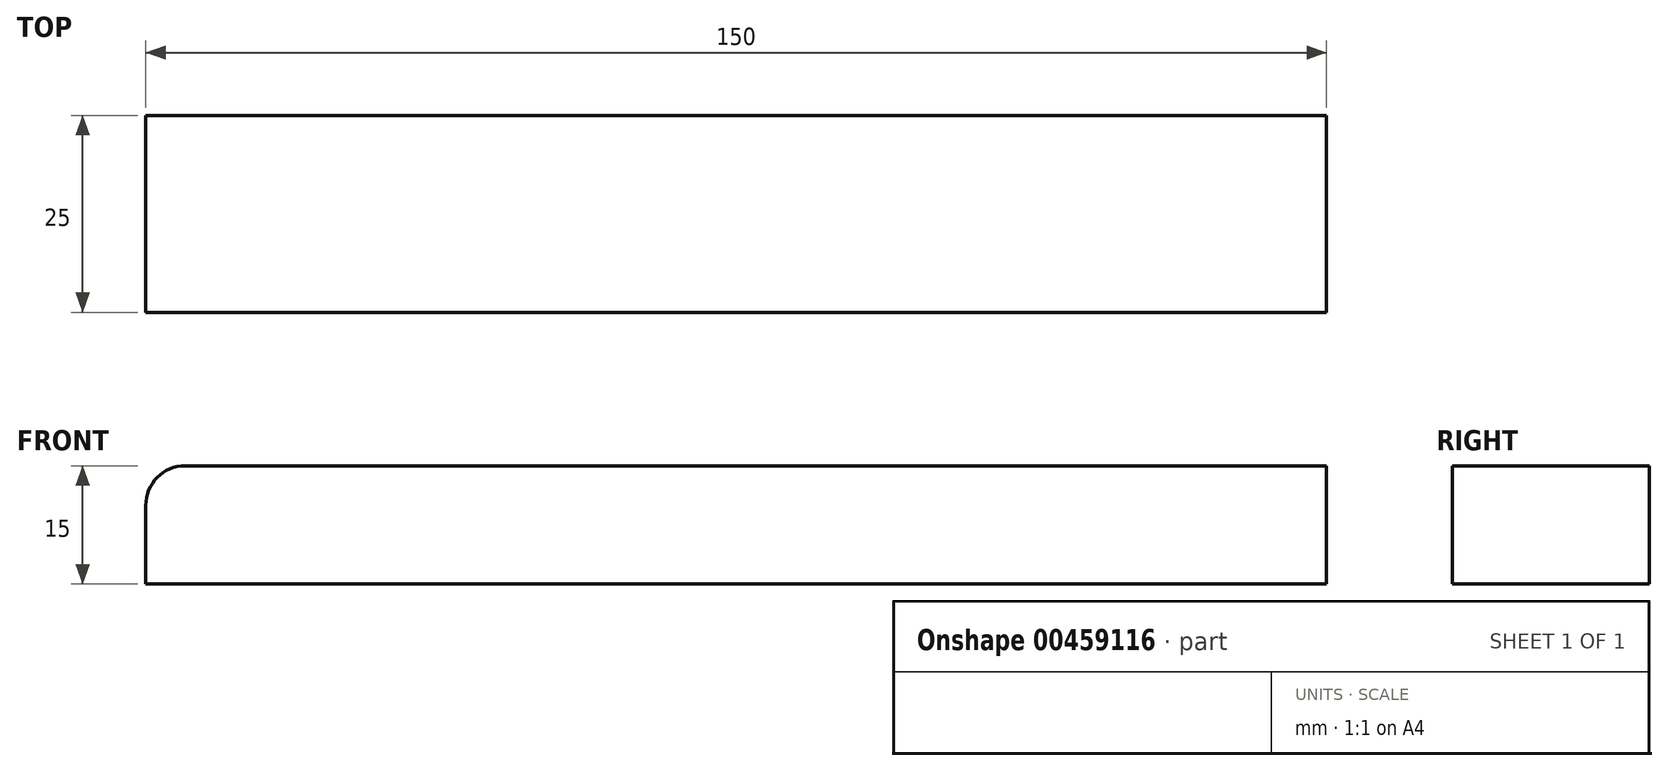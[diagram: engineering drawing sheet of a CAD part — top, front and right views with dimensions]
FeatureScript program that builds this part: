
annotation { "Feature Type Name" : "Feature", "Feature Type Description" : "" }
export const myFeature = defineFeature(function(context is Context, id is Id, definition is map)
    precondition{}
    {
        {
            var Q0;
            Q0=qCreatedBy(makeId("Front.planeOp"),FACE);
            var sketch = newSketch(context, id + "F0", { "sketchPlane" : qUnion([Q0])});
            skLineSegment(sketch, "E0.bottom", {"start": v(-461.04, 0) * mm, "end": v(-381.04, 0) * mm});
            skLineSegment(sketch, "E0.top", {"start": v(-461.04, 15) * mm, "end": v(-381.04, 15) * mm});
            skPoint(sketch, "E1.orphan", {"position": v(385.48, 15) * mm});
            skLineSegment(sketch, "E2", {"start": v(-461.04, 15) * mm, "end": v(-461.04, 0) * mm});
            skPoint(sketch, "E0.right.end.orphan", {"position": v(2.22, 7.5) * mm});
            skPoint(sketch, "E3.end.orphan", {"position": v(492.82, 0) * mm});
            skLineSegment(sketch, "E4", {"start": v(-381.04, 15) * mm, "end": v(-368.44, 15) * mm});
            skLineSegment(sketch, "E5", {"start": v(-368.44, 0) * mm, "end": v(-381.04, 0) * mm});
            skPoint(sketch, "E6.orphan", {"position": v(-377.98, 0) * mm});
            skLineSegment(sketch, "E7", {"start": v(-368.44, 15) * mm, "end": v(-311.04, 15) * mm});
            skLineSegment(sketch, "E8", {"start": v(-368.44, 0) * mm, "end": v(-311.04, 0) * mm});
            skLineSegment(sketch, "E9", {"start": v(-311.04, 0) * mm, "end": v(-311.04, 15) * mm});
            skSolve(sketch);
        }
        {
            var Q0;
            Q0 = qSketchRegion(id + "F0", true);
            extrude(context, id + "F1", {"entities" : qUnion([Q0]), "depth" : 25 * mm, "offsetDistance" : 25 * mm});
        }
        {
            var Q0;
            Q0=makeQuery(id+"F1.opExtrude","SWEPT_EDGE",EDGE,{"disambiguationData":[OSD([sQuery(id+"F0.wireOp",EDGE,"E0.top"),sQuery(id+"F0.wireOp",EDGE,"E2")])]});
            fillet(context, id + "F2", {"entities" : qUnion([Q0]), "radius" : 5 * mm, "tangentPropagation" : true, "allowEdgeOverflow" : false});
        }
    });
